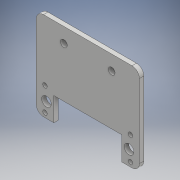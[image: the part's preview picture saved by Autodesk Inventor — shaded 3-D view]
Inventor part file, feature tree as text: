
AUTODESK INVENTOR PART (.ipt)
format: ipt  version: 2017 (Build 210142000, 142)  size: 150,016 bytes
history: native  units: mm
features: fillet x2, sketch x2, extrude x1, hole x1
ambient origin geometry x8: Origin, YZ Plane, XZ Plane, XY Plane, X Axis, Y Axis, Z Axis, Center Point
bodies: Solide1 (feature_tree)
feature tree (6):
  extrude  "Extrusion1"  Depth=60.0mm
  fillet  "Congé1"  Radius=70.0mm
  fillet  "Congé2"  Radius=10.0mm
  hole  "Perçage1"  [1 undecoded]
  sketch  "Esquisse1"
  sketch  "Esquisse2"
note: 1 required parameter value undecoded (feature->parameter linkage not recoverable at this tier; creation-order binding heuristic only, values carry confidence <= 0.55)
